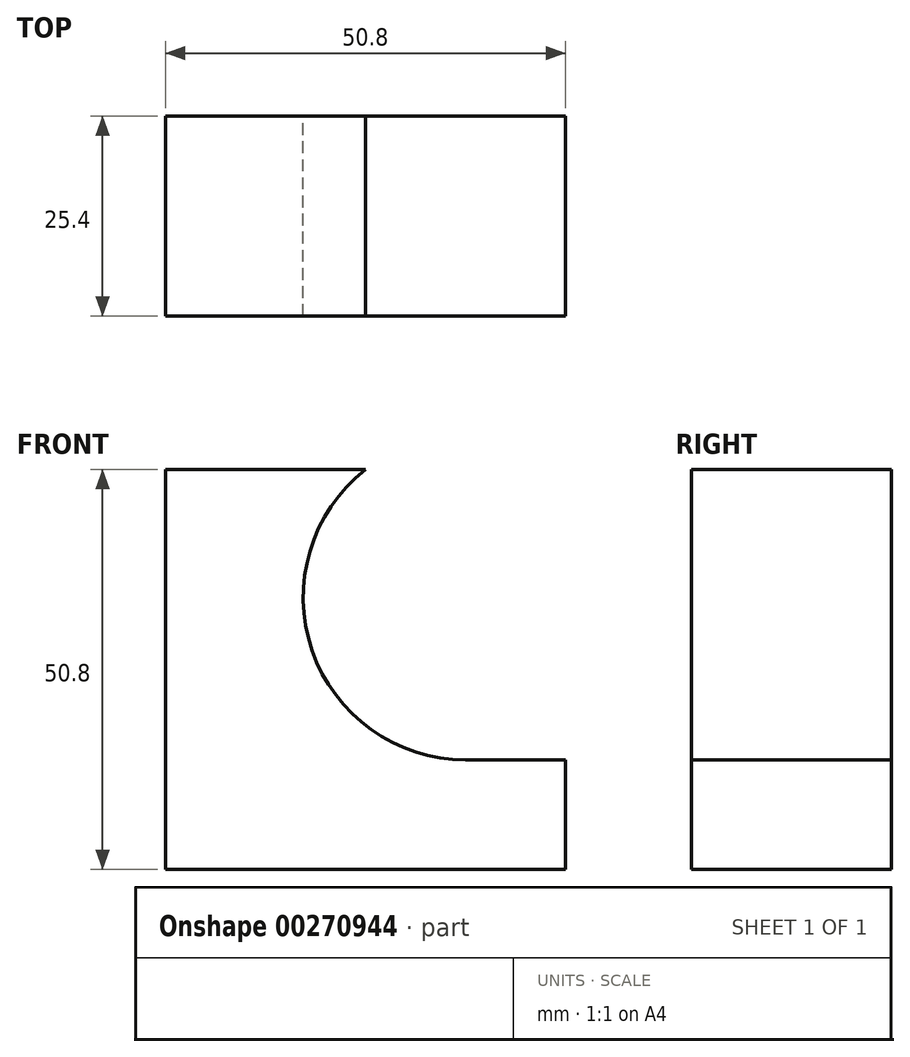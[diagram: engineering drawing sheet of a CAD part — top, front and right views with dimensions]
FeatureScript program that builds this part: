
annotation { "Feature Type Name" : "Feature", "Feature Type Description" : "" }
export const myFeature = defineFeature(function(context is Context, id is Id, definition is map)
    precondition{}
    {
        {
            var Q0;
            Q0=qCreatedBy(makeId("Front.planeOp"),FACE);
            var sketch = newSketch(context, id + "F0", { "sketchPlane" : qUnion([Q0])});
            skLineSegment(sketch, "E0", {"start": v(-8.02, 7.64) * mm, "end": v(-58.82, 7.64) * mm});
            skLineSegment(sketch, "E1", {"start": v(-58.82, 7.64) * mm, "end": v(-58.82, 58.44) * mm});
            skLineSegment(sketch, "E2", {"start": v(-58.82, 58.44) * mm, "end": v(-33.42, 58.44) * mm});
            skLineSegment(sketch, "E3", {"start": v(-8.02, 7.64) * mm, "end": v(-8.02, 21.58) * mm});
            skLineSegment(sketch, "E4", {"start": v(-8.02, 21.58) * mm, "end": v(-20.72, 21.58) * mm});
            skArc(sketch, "E5", {"start": v(-33.42, 58.44) * mm, "mid": v(-40.21, 35.48) * mm, "end": v(-20.72, 21.58) * mm});
            skSolve(sketch);
        }
        {
            var Q0;
            Q0 = qSketchRegion(id + "F0", true);
            extrude(context, id + "F1", {"entities" : qUnion([Q0]), "depth" : 25.4 * mm});
        }
    });
